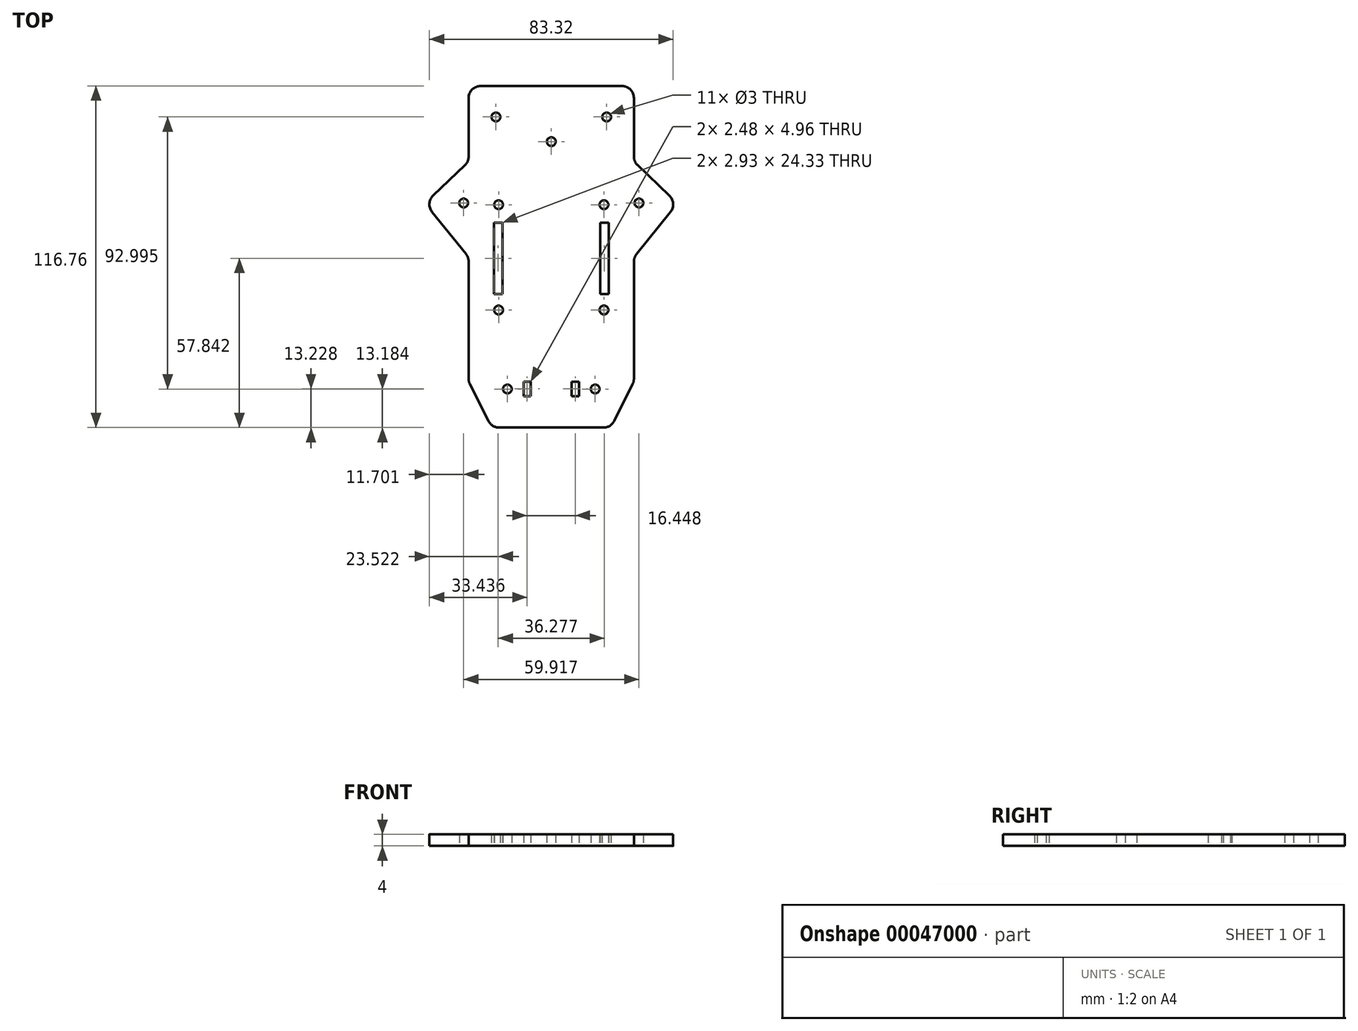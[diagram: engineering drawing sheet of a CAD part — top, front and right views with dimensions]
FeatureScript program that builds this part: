
annotation { "Feature Type Name" : "Feature", "Feature Type Description" : "" }
export const myFeature = defineFeature(function(context is Context, id is Id, definition is map)
    precondition{}
    {
        {
            var Q0;
            Q0=qCreatedBy(makeId("Top.planeOp"),FACE);
            var sketch = newSketch(context, id + "F0", { "sketchPlane" : qUnion([Q0])});
            skLineSegment(sketch, "E0", {"start": v(28.25, 54.46) * mm, "end": v(28.25, 34.46) * mm});
            skLineSegment(sketch, "E1", {"start": v(29.53, 31.47) * mm, "end": v(40.38, 21.12) * mm});
            skLineSegment(sketch, "E2", {"start": v(40.75, 15.55) * mm, "end": v(29.16, 1.13) * mm});
            skLineSegment(sketch, "E3", {"start": v(28.25, -1.45) * mm, "end": v(28.25, -41.45) * mm});
            skLineSegment(sketch, "E4", {"start": v(27.81, -43.3) * mm, "end": v(21.51, -55.9) * mm});
            skLineSegment(sketch, "E5", {"start": v(17.82, -58.18) * mm, "end": v(0, -58.18) * mm});
            skPoint(sketch, "E6.visualSharp", {"position": v(28.25, 58.58) * mm});
            skArc(sketch, "E6.filletArc", {"start": v(28.25, 54.46) * mm, "mid": v(27.04, 57.37) * mm, "end": v(24.12, 58.58) * mm});
            skPoint(sketch, "E7.visualSharp", {"position": v(28.25, -42.43) * mm});
            skArc(sketch, "E7.filletArc", {"start": v(27.81, -43.3) * mm, "mid": v(28.14, -42.4) * mm, "end": v(28.25, -41.45) * mm});
            skPoint(sketch, "E8.visualSharp", {"position": v(20.37, -58.18) * mm});
            skArc(sketch, "E8.filletArc", {"start": v(17.82, -58.18) * mm, "mid": v(20, -57.57) * mm, "end": v(21.51, -55.9) * mm});
            skArc(sketch, "E9.filletArc", {"start": v(29.16, 1.13) * mm, "mid": v(28.48, -0.08) * mm, "end": v(28.25, -1.45) * mm});
            skPoint(sketch, "E10.visualSharp", {"position": v(28.25, 32.7) * mm});
            skArc(sketch, "E10.filletArc", {"start": v(28.25, 34.46) * mm, "mid": v(28.58, 32.83) * mm, "end": v(29.53, 31.47) * mm});
            skPoint(sketch, "E11.visualSharp", {"position": v(43.12, 18.5) * mm});
            skArc(sketch, "E11.filletArc", {"start": v(40.75, 15.55) * mm, "mid": v(41.65, 18.4) * mm, "end": v(40.38, 21.12) * mm});
            skCircle(sketch, "E12", {"center": v(18.93, 48) * mm, "radius": 1.5 * mm});
            skCircle(sketch, "E13", {"center": v(29.96, 18.58) * mm, "radius": 1.5 * mm});
            skCircle(sketch, "E14", {"center": v(15, -45) * mm, "radius": 1.5 * mm});
            skLineSegment(sketch, "E15", {"start": v(24.12, 58.58) * mm, "end": v(0, 58.58) * mm});
            skArc(sketch, "E16.MirrorCS", {"start": v(-28.25, 34.46) * mm, "mid": v(-28.58, 32.83) * mm, "end": v(-29.53, 31.47) * mm});
            skArc(sketch, "E17.MirrorCS", {"start": v(-29.16, 1.13) * mm, "mid": v(-28.48, -0.08) * mm, "end": v(-28.25, -1.45) * mm});
            skArc(sketch, "E18.MirrorCS", {"start": v(-27.81, -43.3) * mm, "mid": v(-28.14, -42.4) * mm, "end": v(-28.25, -41.45) * mm});
            skArc(sketch, "E19.MirrorCS", {"start": v(-17.82, -58.18) * mm, "mid": v(-20, -57.57) * mm, "end": v(-21.51, -55.9) * mm});
            skArc(sketch, "E20.MirrorCS", {"start": v(-40.75, 15.55) * mm, "mid": v(-41.65, 18.4) * mm, "end": v(-40.38, 21.12) * mm});
            skLineSegment(sketch, "E21.MirrorCS", {"start": v(-29.53, 31.47) * mm, "end": v(-40.38, 21.12) * mm});
            skArc(sketch, "E22.MirrorCS", {"start": v(-28.25, 54.46) * mm, "mid": v(-27.04, 57.37) * mm, "end": v(-24.12, 58.58) * mm});
            skPoint(sketch, "E23.MirrorP", {"position": v(-43.12, 18.5) * mm});
            skLineSegment(sketch, "E24.MirrorCS", {"start": v(-28.25, 54.46) * mm, "end": v(-28.25, 34.46) * mm});
            skLineSegment(sketch, "E25.MirrorCS", {"start": v(-17.82, -58.18) * mm, "end": v(0, -58.18) * mm});
            skPoint(sketch, "E26.MirrorP", {"position": v(-20.37, -58.18) * mm});
            skPoint(sketch, "E27.MirrorP", {"position": v(-28.25, -42.43) * mm});
            skPoint(sketch, "E28.MirrorP", {"position": v(-28.25, 0) * mm});
            skCircle(sketch, "E29.MirrorC", {"center": v(-15, -45) * mm, "radius": 1.5 * mm});
            skLineSegment(sketch, "E30.MirrorCS", {"start": v(-24.12, 58.58) * mm, "end": v(0, 58.58) * mm});
            skCircle(sketch, "E31.MirrorC", {"center": v(-18.93, 48) * mm, "radius": 1.5 * mm});
            skLineSegment(sketch, "E32.MirrorCS", {"start": v(-28.25, -1.45) * mm, "end": v(-28.25, -41.45) * mm});
            skPoint(sketch, "E33.MirrorP", {"position": v(-28.25, 58.58) * mm});
            skLineSegment(sketch, "E34.MirrorCS", {"start": v(-27.81, -43.3) * mm, "end": v(-21.51, -55.9) * mm});
            skLineSegment(sketch, "E35.MirrorCS", {"start": v(-40.75, 15.55) * mm, "end": v(-29.16, 1.13) * mm});
            skCircle(sketch, "E36.MirrorC", {"center": v(-29.96, 18.58) * mm, "radius": 1.5 * mm});
            skPoint(sketch, "E37.MirrorP", {"position": v(-28.25, 32.7) * mm});
            skCircle(sketch, "E38", {"center": v(0, 39.55) * mm, "radius": 1.5 * mm});
            skPoint(sketch, "E39.rect.middle", {"position": v(0, 0) * mm});
            skCircle(sketch, "E40", {"center": v(18, 18) * mm, "radius": 1.5 * mm});
            skCircle(sketch, "E41", {"center": v(18, -18) * mm, "radius": 1.5 * mm});
            skCircle(sketch, "E42.MirrorC", {"center": v(-18, -18) * mm, "radius": 1.5 * mm});
            skCircle(sketch, "E43.MirrorC", {"center": v(-18, 18) * mm, "radius": 1.5 * mm});
            skLineSegment(sketch, "E44.bottom", {"start": v(-19.6, 11.83) * mm, "end": v(-16.67, 11.83) * mm});
            skLineSegment(sketch, "E44.top", {"start": v(-19.6, -12.5) * mm, "end": v(-16.67, -12.5) * mm});
            skLineSegment(sketch, "E44.left", {"start": v(-19.6, 11.83) * mm, "end": v(-19.6, -12.5) * mm});
            skLineSegment(sketch, "E44.right", {"start": v(-16.67, 11.83) * mm, "end": v(-16.67, -12.5) * mm});
            skLineSegment(sketch, "E45.MirrorCS", {"start": v(19.6, -12.5) * mm, "end": v(16.67, -12.5) * mm});
            skLineSegment(sketch, "E46.MirrorCS", {"start": v(19.6, 11.83) * mm, "end": v(19.6, -12.5) * mm});
            skLineSegment(sketch, "E47.MirrorCS", {"start": v(16.67, 11.83) * mm, "end": v(16.67, -12.5) * mm});
            skLineSegment(sketch, "E48.MirrorCS", {"start": v(19.6, 11.83) * mm, "end": v(16.67, 11.83) * mm});
            skLineSegment(sketch, "E49.bottom", {"start": v(-9.46, -42.47) * mm, "end": v(-6.98, -42.47) * mm});
            skLineSegment(sketch, "E49.top", {"start": v(-9.46, -47.43) * mm, "end": v(-6.98, -47.43) * mm});
            skLineSegment(sketch, "E49.left", {"start": v(-9.46, -42.47) * mm, "end": v(-9.46, -47.43) * mm});
            skLineSegment(sketch, "E49.right", {"start": v(-6.98, -42.47) * mm, "end": v(-6.98, -47.43) * mm});
            skLineSegment(sketch, "E50.MirrorCS", {"start": v(9.46, -42.47) * mm, "end": v(6.98, -42.47) * mm});
            skLineSegment(sketch, "E51.MirrorCS", {"start": v(9.46, -42.47) * mm, "end": v(9.46, -47.43) * mm});
            skLineSegment(sketch, "E52.MirrorCS", {"start": v(6.98, -42.47) * mm, "end": v(6.98, -47.43) * mm});
            skLineSegment(sketch, "E53.MirrorCS", {"start": v(9.46, -47.43) * mm, "end": v(6.98, -47.43) * mm});
            skLineSegment(sketch, "E54", {"start": v(-15, -45) * mm, "end": v(15, -45) * mm});
            skSolve(sketch);
        }
        {
            var Q0;
            Q0 = qSketchRegion(id + "F0", true);
            extrude(context, id + "F1", {"entities" : qUnion([Q0]), "depth" : 4 * mm});
        }
    });
